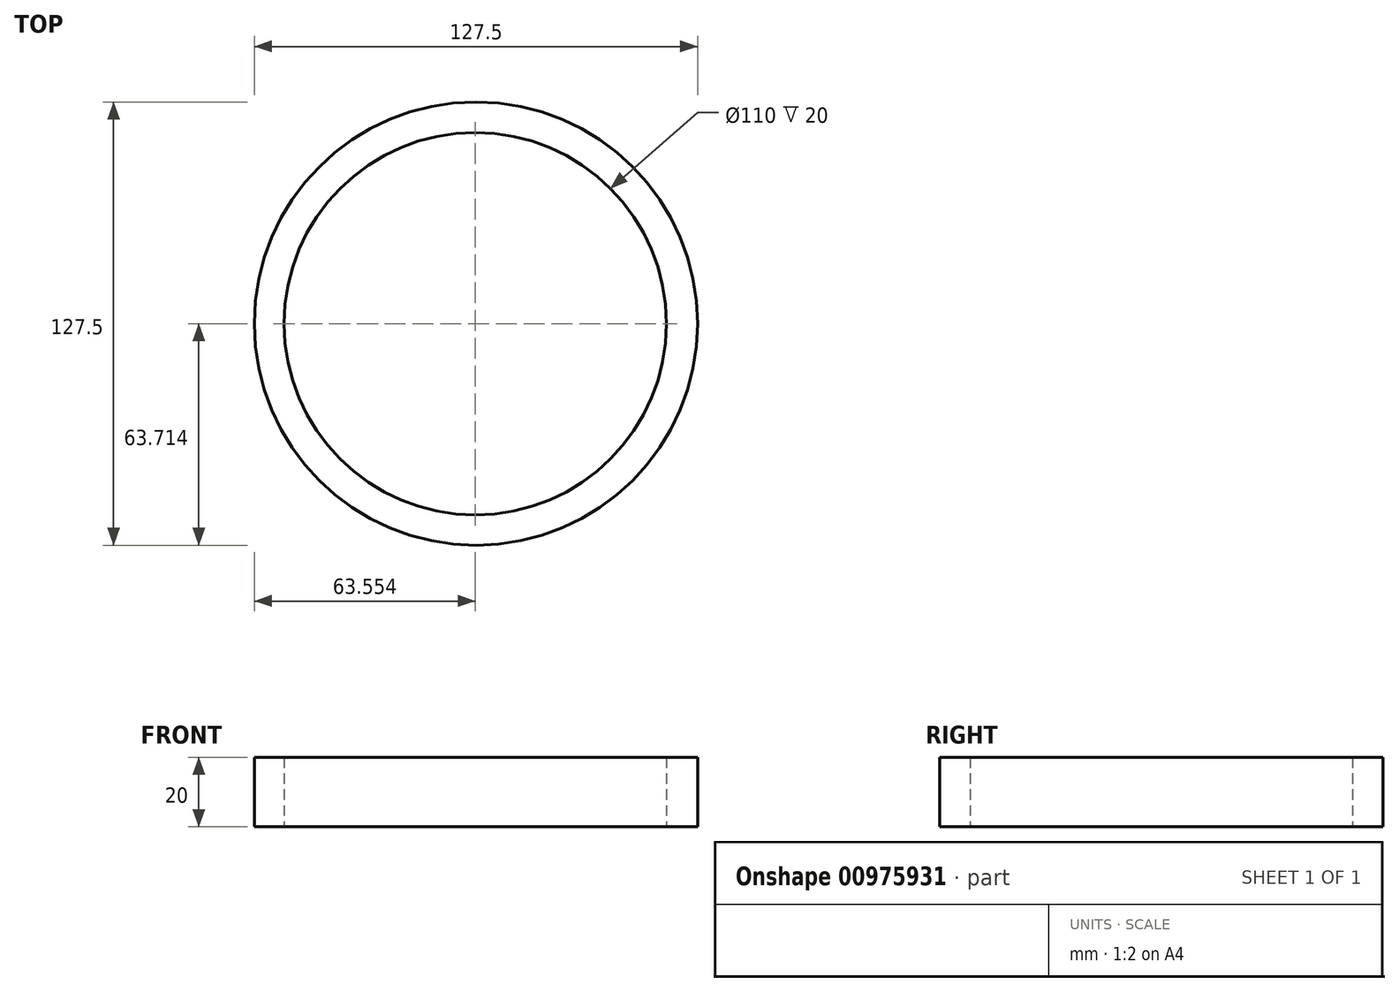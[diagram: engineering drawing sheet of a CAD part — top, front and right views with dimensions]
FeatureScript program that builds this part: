
annotation { "Feature Type Name" : "Feature", "Feature Type Description" : "" }
export const myFeature = defineFeature(function(context is Context, id is Id, definition is map)
    precondition{}
    {
        {
            var Q0;
            Q0=qCreatedBy(makeId("Top.planeOp"),FACE);
            var sketch = newSketch(context, id + "F0", { "sketchPlane" : qUnion([Q0])});
            skCircle(sketch, "E0", {"center": v(0, 0) * mm, "radius": 63.75 * mm});
            skSolve(sketch);
        }
        {
            var Q0;
            Q0 = qSketchRegion(id + "F0", true);
            extrude(context, id + "F1", {"entities" : qUnion([Q0]), "depth" : 20 * mm, "offsetDistance" : 25 * mm});
        }
        {
            var Q0;
            Q0=qCreatedBy(makeId("Top.planeOp"),FACE);
            var sketch = newSketch(context, id + "F2", { "sketchPlane" : qUnion([Q0])});
            skCircle(sketch, "E1", {"center": v(-174, -105.14) * mm, "radius": 55 * mm});
            skSolve(sketch);
        }
        {
            var Q0;
            Q0 = qSketchRegion(id + "F2", true);
            extrude(context, id + "F3", {"entities" : qUnion([Q0]), "depth" : 25 * mm, "offsetDistance" : 25 * mm});
        }
        {
            var Q0;
            Q0=makeQuery(id+"F3.opExtrude","SWEPT_BODY",BODY,{"disambiguationData":[OSD([sQuery(id+"F2.wireOp",EDGE,"E1")])]});
            transform(context, id + "F4", {"entities" : qUnion([Q0]), "transformType" : TransformType.TRANSLATION_3D, "dx" : 173.8 * mm, "dy" : 105.1 * mm, "dz" : -2.2 * mm, "makeCopy" : false});
        }
        {
            var Q0;
            Q0=makeQuery(id+"F3.opExtrude","SWEPT_BODY",BODY,{"disambiguationData":[OSD([sQuery(id+"F2.wireOp",EDGE,"E1")])]});
            var Q1;
            Q1=makeQuery(id+"F1.opExtrude","SWEPT_BODY",BODY,{"disambiguationData":[OSD([sQuery(id+"F0.wireOp",EDGE,"E0")])]});
            booleanBodies(context, id + "F5", {"operationType" : BooleanOperationType.SUBTRACTION, "tools" : qUnion([Q0]), "targets" : qUnion([Q1])});
        }
    });
